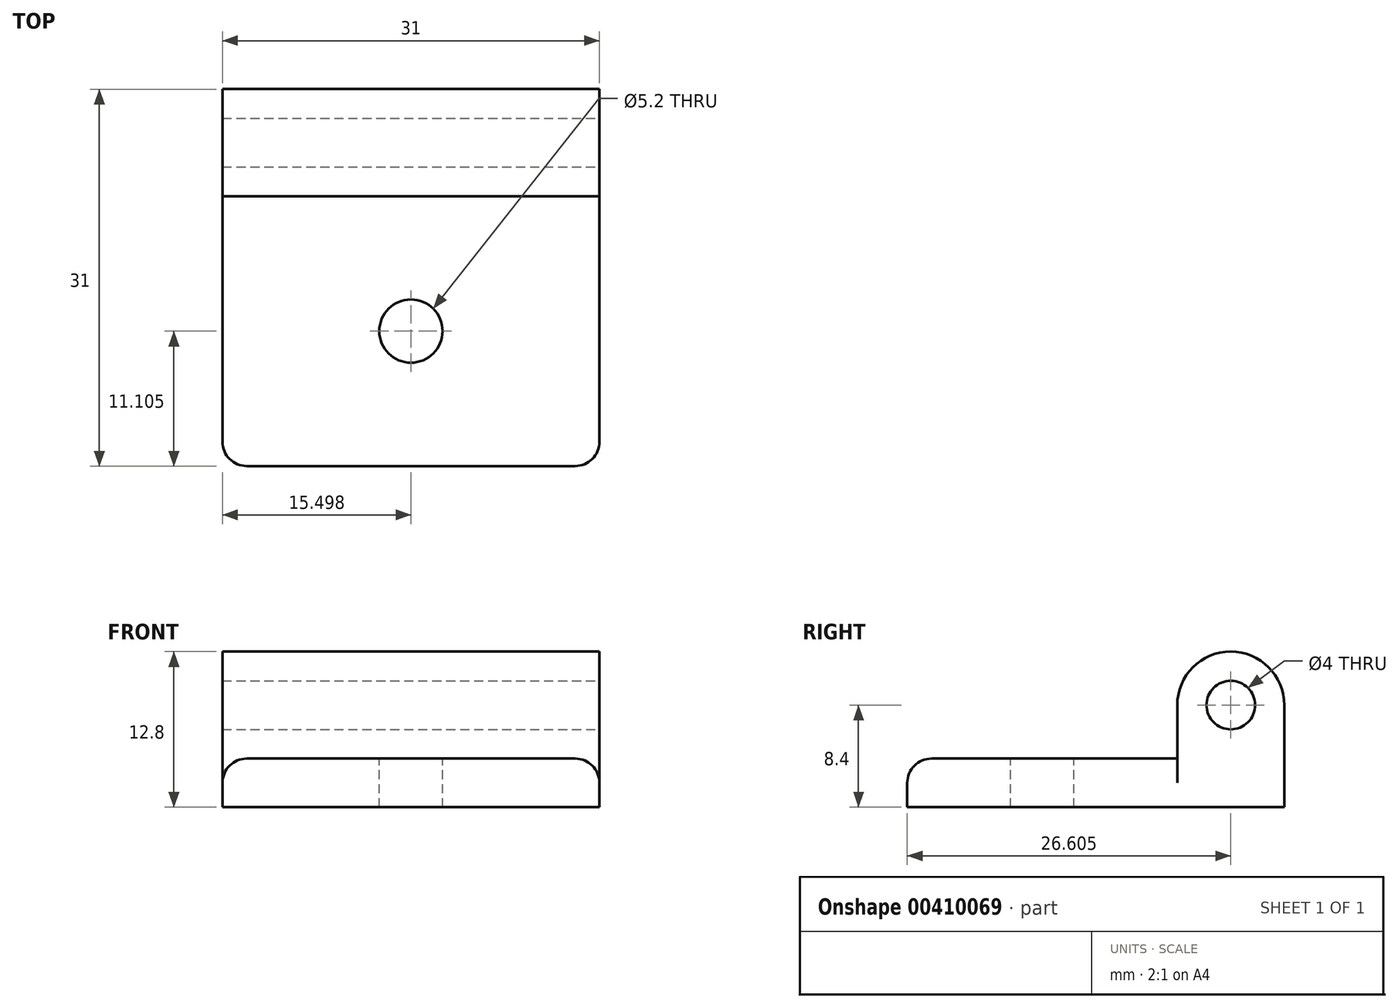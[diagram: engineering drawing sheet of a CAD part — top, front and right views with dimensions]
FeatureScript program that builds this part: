
annotation { "Feature Type Name" : "Feature", "Feature Type Description" : "" }
export const myFeature = defineFeature(function(context is Context, id is Id, definition is map)
    precondition{}
    {
        {
            var Q0;
            Q0=qCreatedBy(makeId("Top.planeOp"),FACE);
            var sketch = newSketch(context, id + "F0", { "sketchPlane" : qUnion([Q0])});
            skLineSegment(sketch, "E0.bottom", {"start": v(-71.77, 53.28) * mm, "end": v(-40.77, 53.28) * mm});
            skLineSegment(sketch, "E0.top", {"start": v(-71.77, 22.28) * mm, "end": v(-40.77, 22.28) * mm});
            skLineSegment(sketch, "E0.left", {"start": v(-71.77, 53.28) * mm, "end": v(-71.77, 22.28) * mm});
            skLineSegment(sketch, "E0.right", {"start": v(-40.77, 53.28) * mm, "end": v(-40.77, 22.28) * mm});
            skLineSegment(sketch, "E1", {"start": v(-71.77, 44.48) * mm, "end": v(-40.77, 44.48) * mm});
            skPoint(sketch, "E1.endSnap0", {"position": v(-40.77, 37.78) * mm});
            skCircle(sketch, "E2", {"center": v(-56.27, 33.38) * mm, "radius": 2.6 * mm});
            skPoint(sketch, "E2.centerSnap0", {"position": v(-56.27, 44.48) * mm});
            skSolve(sketch);
        }
        {
            var Q0;
            Q0 = qSketchRegion(id + "F0", true);
            extrude(context, id + "F1", {"entities" : qUnion([Q0]), "oppositeDirection" : true, "depth" : 4 * mm});
        }
        {
            var Q0;
            {var subQ0=sQuery(id+"F0.wireOp",EDGE,"E0.bottom");Q0=makeQuery(id+"F0.imprint","IMPRINT",FACE,{"disambiguationData":[TD([[makeQuery(id+"F0.imprint","IMPRINT",EDGE,{"derivedFrom":subQ0}),-1.0]])]});}
            extrude(context, id + "F2", {"entities" : qUnion([Q0]), "operationType" : NewBodyOperationType.ADD, "depth" : 4.4 * mm});
        }
        {
            var Q0;
            Q0=makeQuery(id+"F2.opExtrude","CAP_FACE",FACE,{"disambiguationData":[OSD([sQuery(id+"F0.wireOp",EDGE,"E0.bottom"),sQuery(id+"F0.wireOp",EDGE,"E0.left"),sQuery(id+"F0.wireOp",EDGE,"E0.right"),sQuery(id+"F0.wireOp",EDGE,"E1")])],"isStart":false});
            var sketch = newSketch(context, id + "F3", { "sketchPlane" : qUnion([Q0])});
            skLineSegment(sketch, "E3", {"start": v(-40.77, 48.88) * mm, "end": v(-71.77, 48.88) * mm});
            skSolve(sketch);
        }
        {
            var Q0;
            {var subQ0=sQuery(id+"F3.wireOp",EDGE,"E3");Q0=makeQuery(id+"F3.imprint","IMPRINT",FACE,{"disambiguationData":[TD([[makeQuery(id+"F3.imprint","IMPRINT",EDGE,{"derivedFrom":subQ0}),1.0]])]});}
            var Q1;
            Q1=sQuery(id+"F3.wireOp",EDGE,"E3");
            revolve(context, id + "F4", {"operationType" : NewBodyOperationType.ADD, "entities" : qUnion([Q0]), "axis" : qUnion([Q1]), "revolveType" : RevolveType.FULL});
        }
        {
            var Q0;
            {var subQ0=sQuery(id+"F0.wireOp",EDGE,"E0.right");Q0=makeQuery(id+"F4.boolean.opBoolean","MERGE",FACE,{"derivedFrom":[makeQuery(id+"F2.boolean.opBoolean","MERGE",FACE,{"derivedFrom":[makeQuery(id+"F1.opExtrude","SWEPT_FACE",FACE,{"disambiguationData":[OSD([subQ0])]}),makeQuery(id+"F2.opExtrude","SWEPT_FACE",FACE,{"disambiguationData":[OSD([subQ0])]})]}),makeQuery(id+"F4.opRevolve","SWEPT_FACE",FACE,{"disambiguationData":[OSD([subQ0])]})]});}
            var sketch = newSketch(context, id + "F5", { "sketchPlane" : qUnion([Q0])});
            skCircle(sketch, "E4", {"center": v(48.88, 4.4) * mm, "radius": 2 * mm});
            skSolve(sketch);
        }
        {
            var Q0;
            Q0=makeQuery(id+"F5.imprint","IMPRINT",FACE,{"disambiguationData":[TD([[makeQuery(id+"F5.imprint","IMPRINT",EDGE,{"derivedFrom":sQuery(id+"F5.wireOp",EDGE,"E4")}),1.0]])]});
            extrude(context, id + "F6", {"entities" : qUnion([Q0]), "operationType" : NewBodyOperationType.REMOVE, "endBound" : BoundingType.THROUGH_ALL, "oppositeDirection" : true, "depth" : 25 * mm});
        }
        {
            var Q0;
            Q0=makeQuery(id+"F2.opExtrude","CAP_EDGE",EDGE,{"disambiguationData":[OSD([sQuery(id+"F0.wireOp",EDGE,"E1")])],"isStart":true});
            var Q1;
            Q1=makeQuery(id+"F1.opExtrude","SWEPT_EDGE",EDGE,{"disambiguationData":[OSD([sQuery(id+"F0.wireOp",EDGE,"E0.top"),sQuery(id+"F0.wireOp",EDGE,"E0.right")])]});
            var Q2;
            Q2=makeQuery(id+"F1.opExtrude","SWEPT_EDGE",EDGE,{"disambiguationData":[OSD([sQuery(id+"F0.wireOp",EDGE,"E0.top"),sQuery(id+"F0.wireOp",EDGE,"E0.left")])]});
            var Q3;
            Q3=makeQuery(id+"F1.opExtrude","CAP_EDGE",EDGE,{"disambiguationData":[OSD([sQuery(id+"F0.wireOp",EDGE,"E0.top")])],"isStart":true});
            var Q4;
            Q4=makeQuery(id+"F1.opExtrude","CAP_EDGE",EDGE,{"disambiguationData":[OSD([sQuery(id+"F0.wireOp",EDGE,"E0.right")])],"isStart":true});
            var Q5;
            Q5=makeQuery(id+"F1.opExtrude","CAP_EDGE",EDGE,{"disambiguationData":[OSD([sQuery(id+"F0.wireOp",EDGE,"E0.left")])],"isStart":true});
            fillet(context, id + "F7", {"entities" : qUnion([Q0, Q1, Q2, Q3, Q4, Q5]), "radius" : 2 * mm, "tangentPropagation" : true, "allowEdgeOverflow" : false});
        }
    });
